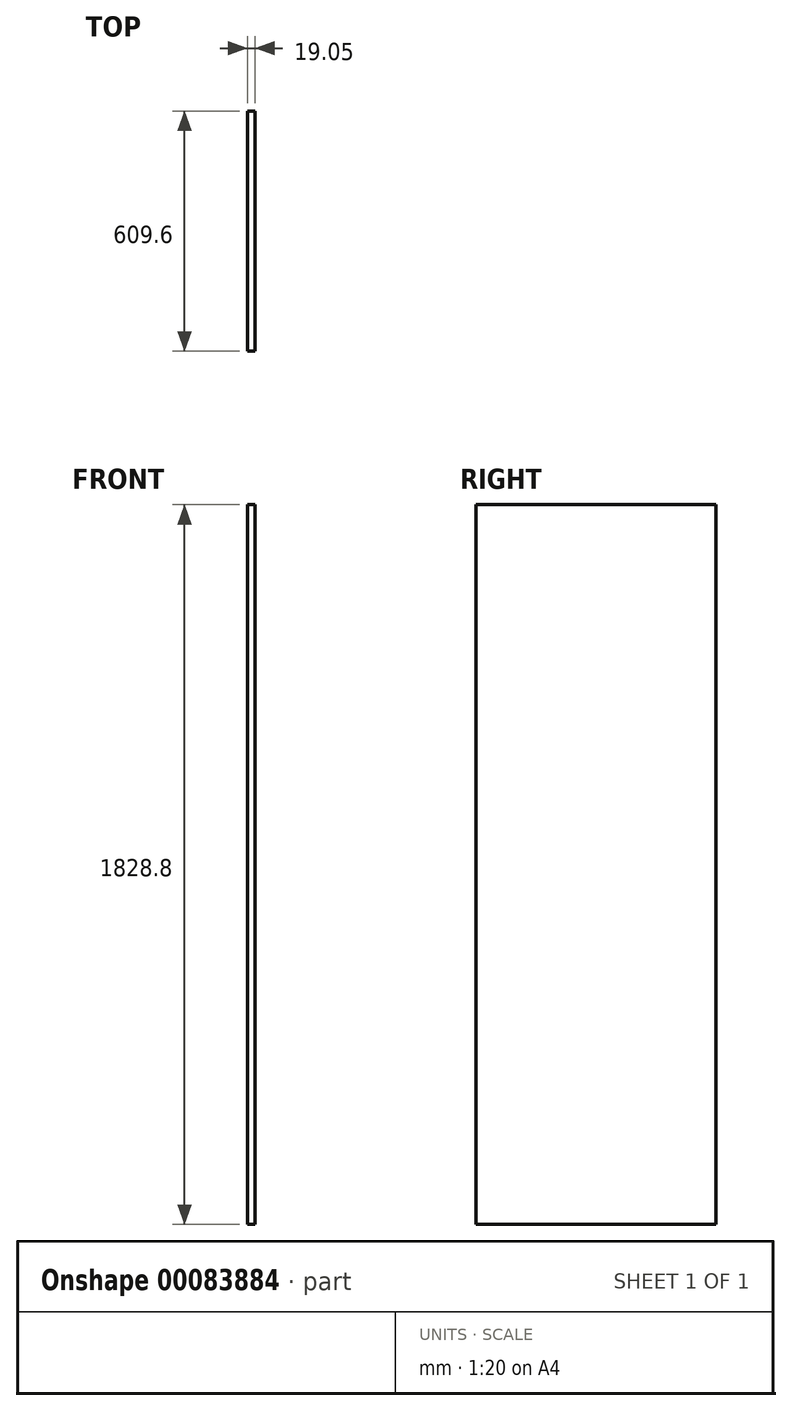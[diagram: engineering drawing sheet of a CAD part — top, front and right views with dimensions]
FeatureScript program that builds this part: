
annotation { "Feature Type Name" : "Feature", "Feature Type Description" : "" }
export const myFeature = defineFeature(function(context is Context, id is Id, definition is map)
    precondition{}
    {
        {
            var Q0;
            Q0=qCreatedBy(makeId("Right.planeOp"),FACE);
            var sketch = newSketch(context, id + "F0", { "sketchPlane" : qUnion([Q0])});
            skLineSegment(sketch, "E0.bottom", {"start": v(304.8, 914.4) * mm, "end": v(-304.8, 914.4) * mm});
            skLineSegment(sketch, "E0.top", {"start": v(304.8, -914.4) * mm, "end": v(-304.8, -914.4) * mm});
            skLineSegment(sketch, "E0.left", {"start": v(304.8, 914.4) * mm, "end": v(304.8, -914.4) * mm});
            skLineSegment(sketch, "E0.right", {"start": v(-304.8, 914.4) * mm, "end": v(-304.8, -914.4) * mm});
            skPoint(sketch, "E0.middle", {"position": v(0, 0) * mm});
            skSolve(sketch);
        }
        {
            var Q0;
            Q0=makeQuery(id+"F0.imprint","IMPRINT",FACE,{"disambiguationData":[TD([[makeQuery(id+"F0.imprint","IMPRINT",EDGE,{"derivedFrom":sQuery(id+"F0.wireOp",EDGE,"E0.bottom")}),1.0]])]});
            extrude(context, id + "F1", {"entities" : qUnion([Q0]), "depth" : 19.05 * mm});
        }
    });
